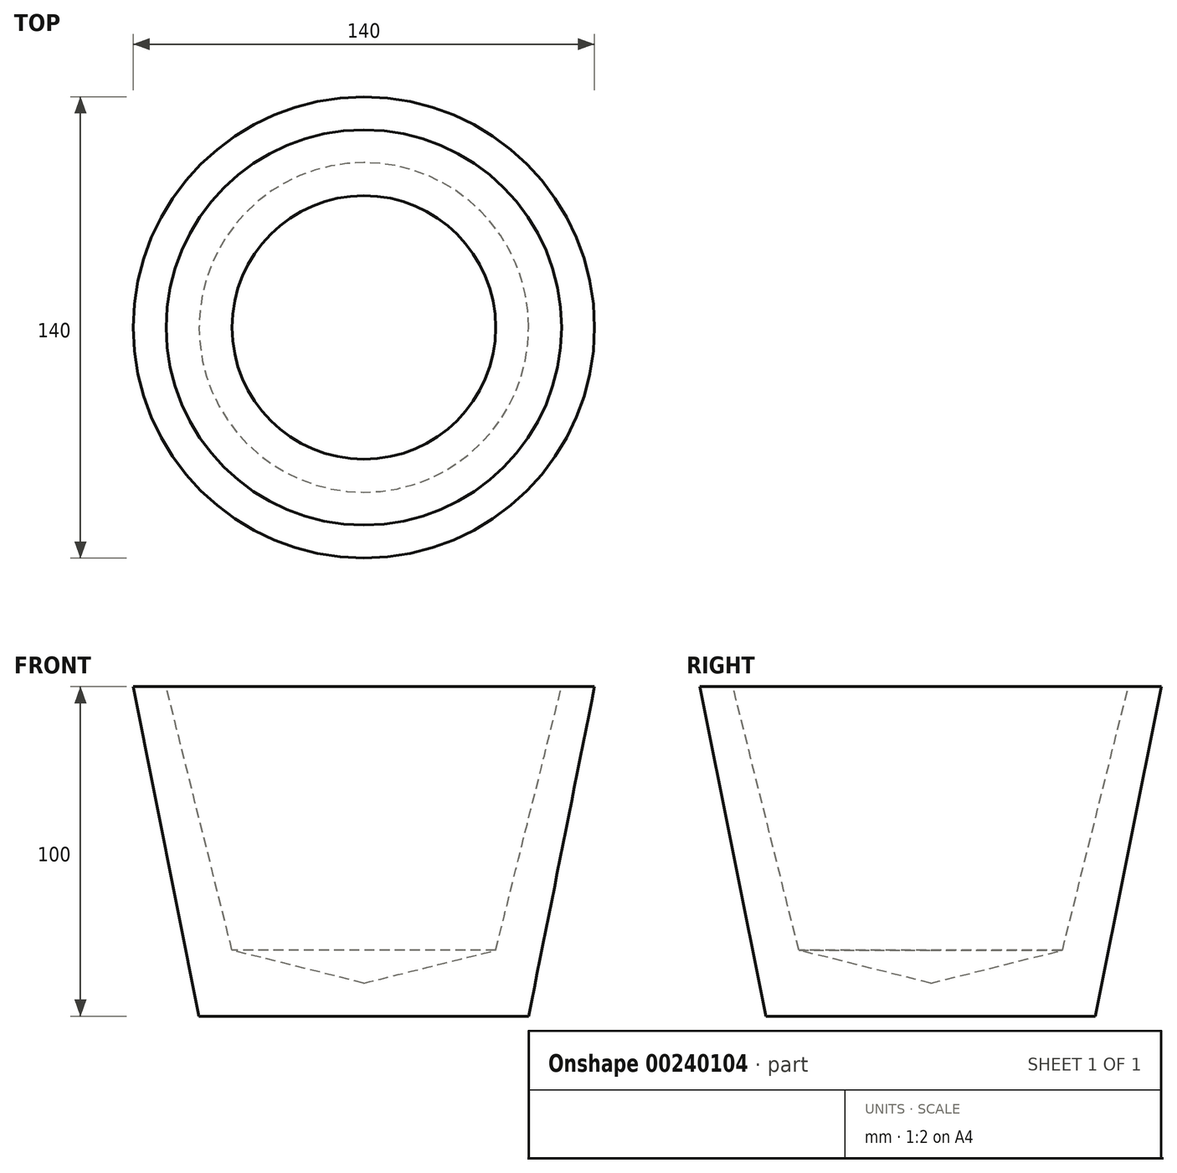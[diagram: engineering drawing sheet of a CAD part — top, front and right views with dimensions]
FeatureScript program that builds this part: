
annotation { "Feature Type Name" : "Feature", "Feature Type Description" : "" }
export const myFeature = defineFeature(function(context is Context, id is Id, definition is map)
    precondition{}
    {
        {
            var Q0;
            Q0=qCreatedBy(makeId("Right.planeOp"),FACE);
            var sketch = newSketch(context, id + "F0", { "sketchPlane" : qUnion([Q0])});
            skLineSegment(sketch, "E0", {"start": v(-70, 100) * mm, "end": v(-60, 100) * mm});
            skLineSegment(sketch, "E1", {"start": v(-60, 100) * mm, "end": v(-40, 20) * mm});
            skLineSegment(sketch, "E2", {"start": v(-40, 20) * mm, "end": v(0, 10) * mm});
            skLineSegment(sketch, "E3", {"start": v(0, 10) * mm, "end": v(0, 0) * mm});
            skLineSegment(sketch, "E4", {"start": v(0, 0) * mm, "end": v(-50, 0) * mm});
            skLineSegment(sketch, "E5", {"start": v(-50, 0) * mm, "end": v(-70, 100) * mm});
            skSolve(sketch);
        }
        {
            var Q0;
            Q0=makeQuery(id+"F0.imprint","IMPRINT",FACE,{"disambiguationData":[TD([[makeQuery(id+"F0.imprint","IMPRINT",EDGE,{"derivedFrom":sQuery(id+"F0.wireOp",EDGE,"E0")}),-1.0]])]});
            var Q1;
            Q1=sQuery(id+"F0.wireOp",EDGE,"E3");
            revolve(context, id + "F1", {"entities" : qUnion([Q0]), "axis" : qUnion([Q1]), "revolveType" : RevolveType.FULL});
        }
    });
